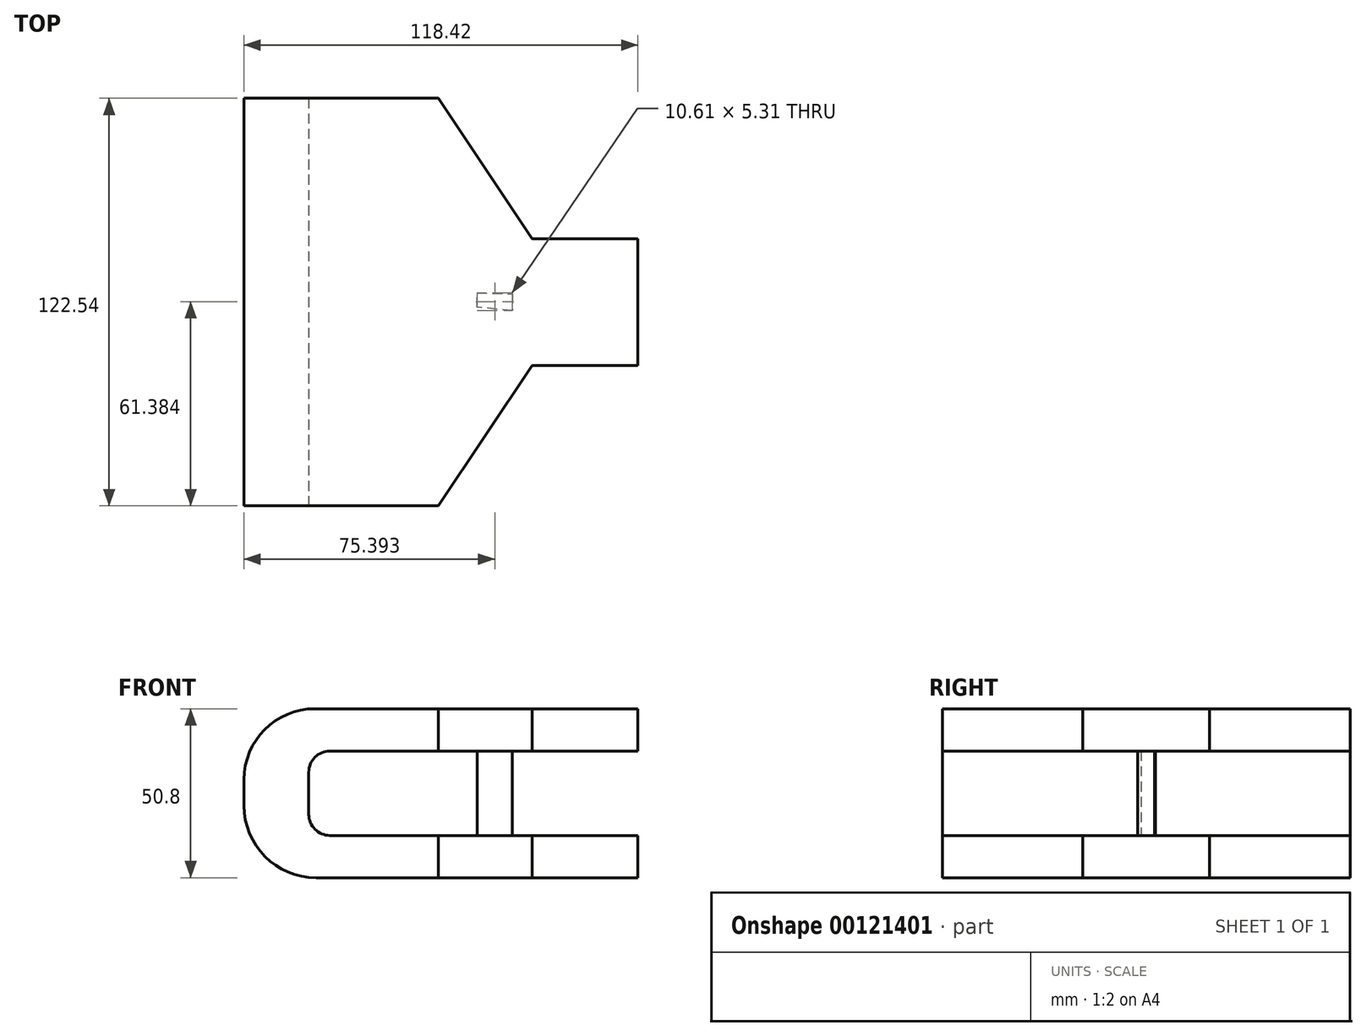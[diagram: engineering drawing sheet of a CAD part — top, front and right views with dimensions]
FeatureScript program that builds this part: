
annotation { "Feature Type Name" : "Feature", "Feature Type Description" : "" }
export const myFeature = defineFeature(function(context is Context, id is Id, definition is map)
    precondition{}
    {
        {
            var Q0;
            Q0=qCreatedBy(makeId("Top.planeOp"),FACE);
            var sketch = newSketch(context, id + "F0", { "sketchPlane" : qUnion([Q0])});
            skLineSegment(sketch, "E0.right", {"start": v(68.06, 21.23) * mm, "end": v(68.06, -16.87) * mm});
            skPoint(sketch, "E0.middle", {"position": v(0, 0) * mm});
            skLineSegment(sketch, "E1", {"start": v(68.06, 21.23) * mm, "end": v(36.3, 21.23) * mm});
            skLineSegment(sketch, "E2", {"start": v(36.3, 21.23) * mm, "end": v(8.06, 63.45) * mm});
            skLineSegment(sketch, "E3", {"start": v(8.06, 63.45) * mm, "end": v(-50.36, 63.45) * mm});
            skLineSegment(sketch, "E4", {"start": v(-50.36, 63.45) * mm, "end": v(-50.36, -59.1) * mm});
            skLineSegment(sketch, "E5", {"start": v(-50.36, -59.1) * mm, "end": v(8.06, -59.1) * mm});
            skLineSegment(sketch, "E6", {"start": v(8.06, -59.1) * mm, "end": v(36.3, -16.87) * mm});
            skLineSegment(sketch, "E7", {"start": v(36.3, -16.87) * mm, "end": v(68.06, -16.87) * mm});
            skPoint(sketch, "E0.bottom.start.orphan", {"position": v(-68.06, 77.2) * mm});
            skPoint(sketch, "E0.top.start.orphan", {"position": v(-68.06, -77.02) * mm});
            skPoint(sketch, "E8.orphan", {"position": v(68.06, -77.2) * mm});
            skPoint(sketch, "E9.orphan", {"position": v(68.06, 77.02) * mm});
            skSolve(sketch);
        }
        {
            var Q0;
            Q0=makeQuery(id+"F0.imprint","IMPRINT",FACE,{"disambiguationData":[TD([[makeQuery(id+"F0.imprint","IMPRINT",EDGE,{"derivedFrom":sQuery(id+"F0.wireOp",EDGE,"E0.right")}),-1.0]])]});
            extrude(context, id + "F1", {"entities" : qUnion([Q0]), "depth" : 50.8 * mm});
        }
        {
            var Q0;
            Q0=makeQuery(id+"F1.opExtrude","CAP_EDGE",EDGE,{"disambiguationData":[OSD([sQuery(id+"F0.wireOp",EDGE,"E4")])],"isStart":true});
            fillet(context, id + "F2", {"entities" : qUnion([Q0]), "radius" : 21.7 * mm, "tangentPropagation" : true, "allowEdgeOverflow" : false});
        }
        {
            var Q0;
            Q0=makeQuery(id+"F1.opExtrude","CAP_EDGE",EDGE,{"disambiguationData":[OSD([sQuery(id+"F0.wireOp",EDGE,"E4")])],"isStart":false});
            fillet(context, id + "F3", {"entities" : qUnion([Q0]), "radius" : 21.32 * mm, "tangentPropagation" : true, "allowEdgeOverflow" : false});
        }
        {
            var Q0;
            Q0=makeQuery(id+"F1.opExtrude","SWEPT_FACE",FACE,{"disambiguationData":[OSD([sQuery(id+"F0.wireOp",EDGE,"E5")])]});
            var sketch = newSketch(context, id + "F4", { "sketchPlane" : qUnion([Q0])});
            skLineSegment(sketch, "E10", {"start": v(8.06, 38.1) * mm, "end": v(-24.52, 38.1) * mm});
            skLineSegment(sketch, "E11", {"start": v(-30.87, 31.75) * mm, "end": v(-30.87, 19.05) * mm});
            skLineSegment(sketch, "E12", {"start": v(-24.52, 12.7) * mm, "end": v(8.06, 12.7) * mm});
            skPoint(sketch, "E13.visualSharp", {"position": v(-30.87, 38.1) * mm});
            skArc(sketch, "E13.filletArc", {"start": v(-24.52, 38.1) * mm, "mid": v(-29.01, 36.24) * mm, "end": v(-30.87, 31.75) * mm});
            skPoint(sketch, "E14.visualSharp", {"position": v(-30.87, 12.7) * mm});
            skArc(sketch, "E14.filletArc", {"start": v(-30.87, 19.05) * mm, "mid": v(-29.01, 14.56) * mm, "end": v(-24.52, 12.7) * mm});
            skLineSegment(sketch, "E15", {"start": v(8.06, 38.1) * mm, "end": v(99.39, 38.1) * mm});
            skLineSegment(sketch, "E16", {"start": v(8.06, 12.7) * mm, "end": v(99.39, 12.7) * mm});
            skLineSegment(sketch, "E17", {"start": v(99.39, 12.7) * mm, "end": v(99.39, 38.1) * mm});
            skSolve(sketch);
        }
        {
            var Q0;
            Q0 = qSketchRegion(id + "F4", true);
            var Q1;
            {var subQ1=sQuery(id+"F4.wireOp",EDGE,"E10");Q1=makeQuery(id+"F4.imprint","IMPRINT",FACE,{"disambiguationData":[TD([[makeQuery(id+"F4.imprint","IMPRINT",EDGE,{"derivedFrom":subQ1}),1.0]])]});}
            extrude(context, id + "F5", {"entities" : qUnion([Q0, Q1]), "operationType" : NewBodyOperationType.REMOVE, "oppositeDirection" : true, "depth" : 157.7 * mm});
        }
        {
            var Q0;
            Q0=makeQuery(id+"F5.boolean.opBoolean","COPY",FACE,{"derivedFrom":makeQuery(id+"F5.opExtrude","SWEPT_FACE",FACE,{"disambiguationData":[OSD([sQuery(id+"F4.wireOp",EDGE,"E12"),sQuery(id+"F4.wireOp",EDGE,"E16")])]})});
            var sketch = newSketch(context, id + "F6", { "sketchPlane" : qUnion([Q0])});
            skLineSegment(sketch, "E18", {"start": v(19.73, 0.6) * mm, "end": v(19.73, 4.95) * mm});
            skLineSegment(sketch, "E19", {"start": v(19.73, 4.95) * mm, "end": v(30.34, 4.72) * mm});
            skLineSegment(sketch, "E20", {"start": v(30.34, 4.72) * mm, "end": v(30.34, -0.36) * mm});
            skLineSegment(sketch, "E21", {"start": v(30.34, -0.36) * mm, "end": v(19.73, 0.6) * mm});
            skSolve(sketch);
        }
        {
            var Q0;
            Q0=makeQuery(id+"F6.imprint","IMPRINT",FACE,{"disambiguationData":[TD([[makeQuery(id+"F6.imprint","IMPRINT",EDGE,{"derivedFrom":sQuery(id+"F6.wireOp",EDGE,"E18")}),-1.0]])]});
            extrude(context, id + "F7", {"entities" : qUnion([Q0]), "operationType" : NewBodyOperationType.ADD, "depth" : 29.05 * mm});
        }
    });
